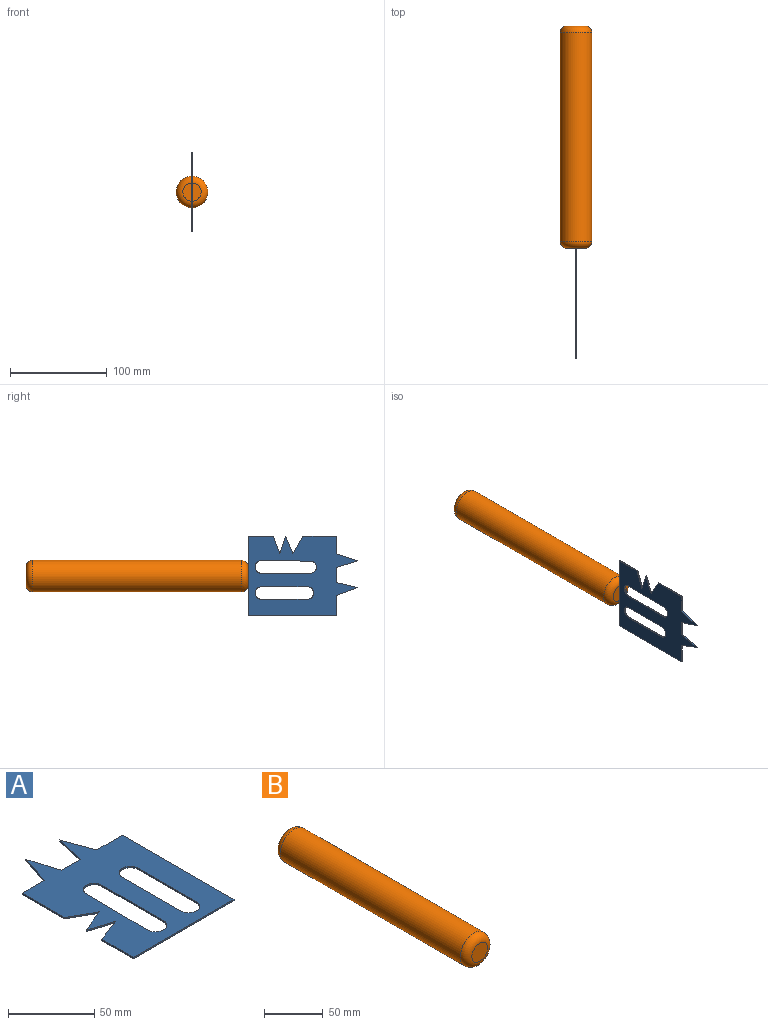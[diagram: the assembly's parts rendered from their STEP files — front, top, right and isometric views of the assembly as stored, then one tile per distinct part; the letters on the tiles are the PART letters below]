
ASSEMBLY  parts=2 mates=1
PART A: 25 faces, bbox 82.5x113.8x1 mm
  f0: plane 22.36x8.18mm, normal (0.94,0.34,0), area 23.8mm2, adj f1,f22,f23,f24
  f1: plane 22.36x5.11mm, normal (-0.97,0.22,0), area 22.9mm2, adj f0,f2,f23,f24
  f2: plane 15.59x1mm, normal (0,1,0), area 15.6mm2, adj f1,f3,f23,f24
  f3: plane 22.36x6.9mm, normal (0.96,0.29,0), area 23.4mm2, adj f2,f4,f23,f24
  f4: plane 22.36x7.16mm, normal (-0.95,0.3,0), area 23.5mm2, adj f3,f5,f23,f24
  f5: plane 18.4x1mm, normal (0,1,0), area 18.4mm2, adj f4,f6,f23,f24
  f6: plane 34.75x1mm, normal (-1,0,0), area 34.8mm2, adj f5,f7,f23,f24
  f7: plane 18.4x10.22mm, normal (-0.49,-0.87,0), area 21.1mm2, adj f6,f8,f23,f24
  f8: plane 18.4x7.67mm, normal (-0.38,0.92,0), area 19.9mm2, adj f7,f9,f23,f24
  f9: plane 18.4x5.89mm, normal (-0.3,-0.95,0), area 19.3mm2, adj f8,f10,f23,f24
  f10: plane 18.4x6.89mm, normal (-0.35,0.94,0), area 19.6mm2, adj f9,f11,f23,f24
  f11: plane 26.04x1mm, normal (-1,0,0), area 26mm2, adj f10,f12,f23,f24
  f12: plane 82.46x1mm, normal (0,-1,0), area 82.5mm2, adj f11,f13,f23,f24
  f13: plane 91.46x1mm, normal (1,0,0), area 91.5mm2, adj f12,f22,f23,f24
  f14: cylinder r=6.36mm len=12.72mm, axis (0,0,-1), area 21.4mm2, adj f15,f20,f23,f24
  f15: plane 49.71x1mm, normal (-1,0,0), area 49.7mm2, adj f14,f16,f23,f24
  f16: cylinder r=6.65mm len=13.3mm, axis (0,0,-1), area 20.9mm2, adj f15,f20,f23,f24
  f17: cylinder r=6.49mm len=12.87mm, axis (0,0,-1), area 18.8mm2, adj f18,f21,f23,f24
  f18: plane 48.54x1mm, normal (-1,0,0), area 48.5mm2, adj f17,f19,f23,f24
  f19: cylinder r=6.44mm len=12.87mm, axis (0,0,-1), area 20.2mm2, adj f18,f21,f23,f24
  f20: plane 49.84x1mm, normal (1,-0.01,0), area 49.8mm2, adj f14,f16,f23,f24
  f21: plane 48.54x1mm, normal (1,0,0), area 48.5mm2, adj f17,f19,f23,f24
  f22: plane 21.12x1mm, normal (0,1,0), area 21.1mm2, adj f0,f13,f23,f24
  f23: plane 113.82x82.46mm, normal (0,0,1), area 6032mm2, adj f0,f1,f2,f3,f4,f5,f6,f7
  f24: plane 113.82x82.46mm, normal (0,0,-1), area 6032mm2, adj f0,f1,f2,f3,f4,f5,f6,f7
PART B: 5 faces, bbox 35.6x230x35.6 mm
  f0: cylinder r=16.45mm len=216mm, axis (0,1,0), area 22327.5mm2, adj f3,f4
  f1: plane 18.9x18.9mm, normal (0,-1,0), area 280.6mm2, adj f4
  f2: plane 18.9x18.9mm, normal (0,1,0), area 280.6mm2, adj f3
  f3: torus R=9.45mm, axis (0,-1,0), area 960.9mm2, adj f0,f2
  f4: torus R=9.45mm, axis (0,-1,0), area 960.9mm2, adj f0,f1
PLACE A rot(axis=(0.71,0,-0.71),180deg) t=(-46.16,-318.64,-25.1)mm
PLACE B t=(-46.66,-49.82,-33.87)mm
MATE fastened A.f12 <-> B.f0  axis (0,1,0) through (-46.66,-279.82,-33.87)mm
